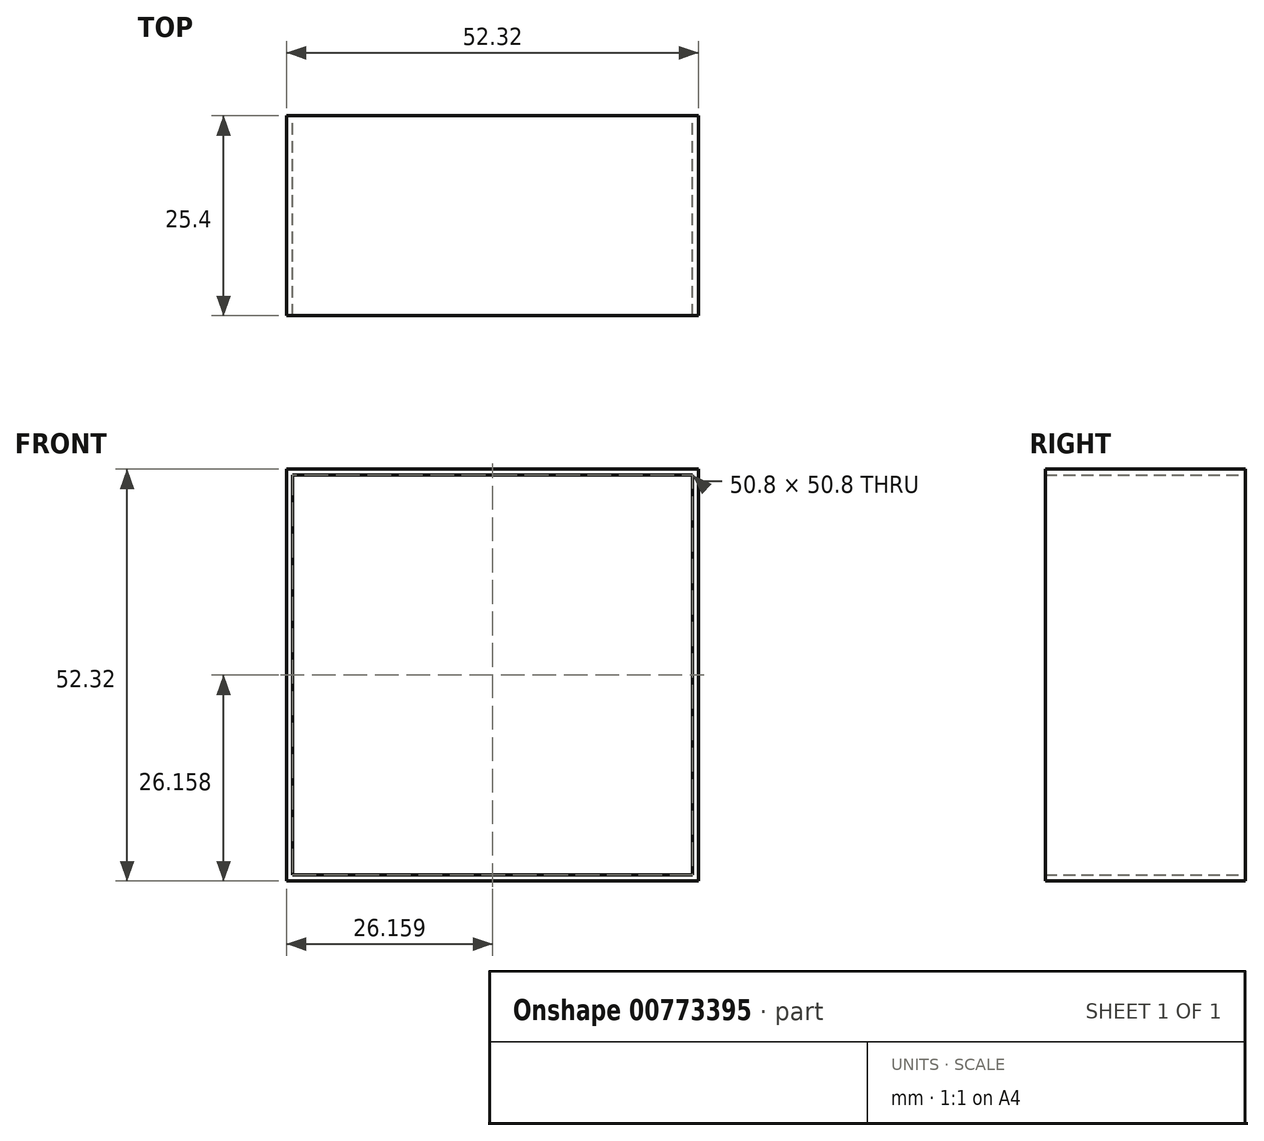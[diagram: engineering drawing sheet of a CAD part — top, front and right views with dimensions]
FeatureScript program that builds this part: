
annotation { "Feature Type Name" : "Feature", "Feature Type Description" : "" }
export const myFeature = defineFeature(function(context is Context, id is Id, definition is map)
    precondition{}
    {
        {
            var Q0;
            Q0=qCreatedBy(makeId("Front.planeOp"),FACE);
            var sketch = newSketch(context, id + "F0", { "sketchPlane" : qUnion([Q0])});
            skLineSegment(sketch, "E0.bottom", {"start": v(-88.76, 59.63) * mm, "end": v(-37.96, 59.63) * mm});
            skLineSegment(sketch, "E0.top", {"start": v(-88.76, 8.83) * mm, "end": v(-37.96, 8.83) * mm});
            skLineSegment(sketch, "E0.left", {"start": v(-88.76, 59.63) * mm, "end": v(-88.76, 8.83) * mm});
            skLineSegment(sketch, "E0.right", {"start": v(-37.96, 59.63) * mm, "end": v(-37.96, 8.83) * mm});
            skLineSegment(sketch, "E1.0", {"start": v(-37.2, 60.4) * mm, "end": v(-37.2, 8.07) * mm});
            skLineSegment(sketch, "E1.1", {"start": v(-89.52, 60.4) * mm, "end": v(-37.2, 60.4) * mm});
            skLineSegment(sketch, "E1.2", {"start": v(-89.52, 60.4) * mm, "end": v(-89.52, 8.07) * mm});
            skLineSegment(sketch, "E1.3", {"start": v(-89.52, 8.07) * mm, "end": v(-37.2, 8.07) * mm});
            skLineSegment(sketch, "E2", {"start": v(-63.36, 59.63) * mm, "end": v(-63.36, 8.83) * mm});
            skLineSegment(sketch, "E3", {"start": v(-63.36, 69.1) * mm, "end": v(-50.66, 69.1) * mm, "construction": true});
            skLineSegment(sketch, "E4", {"start": v(-50.66, 59.63) * mm, "end": v(-50.66, 8.83) * mm});
            skLineSegment(sketch, "E5", {"start": v(-63.36, 69.1) * mm, "end": v(-76.06, 69.1) * mm, "construction": true});
            skLineSegment(sketch, "E6", {"start": v(-76.06, 59.63) * mm, "end": v(-76.06, 8.83) * mm});
            skLineSegment(sketch, "E7.0", {"start": v(-76.82, 59.63) * mm, "end": v(-76.82, 8.83) * mm});
            skLineSegment(sketch, "E8.0", {"start": v(-64.12, 59.63) * mm, "end": v(-64.12, 8.83) * mm});
            skLineSegment(sketch, "E9.0", {"start": v(-51.42, 59.63) * mm, "end": v(-51.42, 8.83) * mm});
            skLineSegment(sketch, "E10", {"start": v(-76.06, 59.63) * mm, "end": v(-76.06, 60.4) * mm});
            skLineSegment(sketch, "E11", {"start": v(-76.06, 60.4) * mm, "end": v(-76.82, 60.4) * mm});
            skLineSegment(sketch, "E12", {"start": v(-76.82, 60.4) * mm, "end": v(-76.82, 59.63) * mm});
            skLineSegment(sketch, "E13", {"start": v(-63.36, 59.63) * mm, "end": v(-63.36, 60.4) * mm});
            skLineSegment(sketch, "E14", {"start": v(-63.36, 60.4) * mm, "end": v(-64.12, 60.4) * mm});
            skLineSegment(sketch, "E15", {"start": v(-50.66, 59.63) * mm, "end": v(-50.66, 60.4) * mm});
            skLineSegment(sketch, "E16", {"start": v(-50.66, 60.4) * mm, "end": v(-51.42, 60.4) * mm});
            skLineSegment(sketch, "E17", {"start": v(-51.42, 60.4) * mm, "end": v(-51.42, 59.63) * mm});
            skLineSegment(sketch, "E18", {"start": v(-64.12, 59.63) * mm, "end": v(-64.12, 60.4) * mm});
            skLineSegment(sketch, "E19", {"start": v(-76.82, 8.83) * mm, "end": v(-76.82, 8.07) * mm});
            skLineSegment(sketch, "E20", {"start": v(-76.82, 8.07) * mm, "end": v(-76.06, 8.07) * mm});
            skLineSegment(sketch, "E21", {"start": v(-76.06, 8.07) * mm, "end": v(-76.06, 8.83) * mm});
            skLineSegment(sketch, "E22", {"start": v(-64.12, 8.83) * mm, "end": v(-64.12, 8.07) * mm});
            skLineSegment(sketch, "E23", {"start": v(-64.12, 8.07) * mm, "end": v(-63.36, 8.07) * mm});
            skLineSegment(sketch, "E24", {"start": v(-63.36, 8.07) * mm, "end": v(-63.36, 8.83) * mm});
            skLineSegment(sketch, "E25", {"start": v(-51.42, 8.83) * mm, "end": v(-51.42, 8.07) * mm});
            skLineSegment(sketch, "E26", {"start": v(-51.42, 8.07) * mm, "end": v(-50.66, 8.07) * mm});
            skLineSegment(sketch, "E27", {"start": v(-50.66, 8.07) * mm, "end": v(-50.66, 8.83) * mm});
            skSolve(sketch);
        }
        {
            var Q0;
            Q0 = qSketchRegion(id + "F0", true);
            extrude(context, id + "F1", {"entities" : qUnion([Q0]), "depth" : 25.4 * mm, "offsetDistance" : 25.4 * mm});
        }
    });
